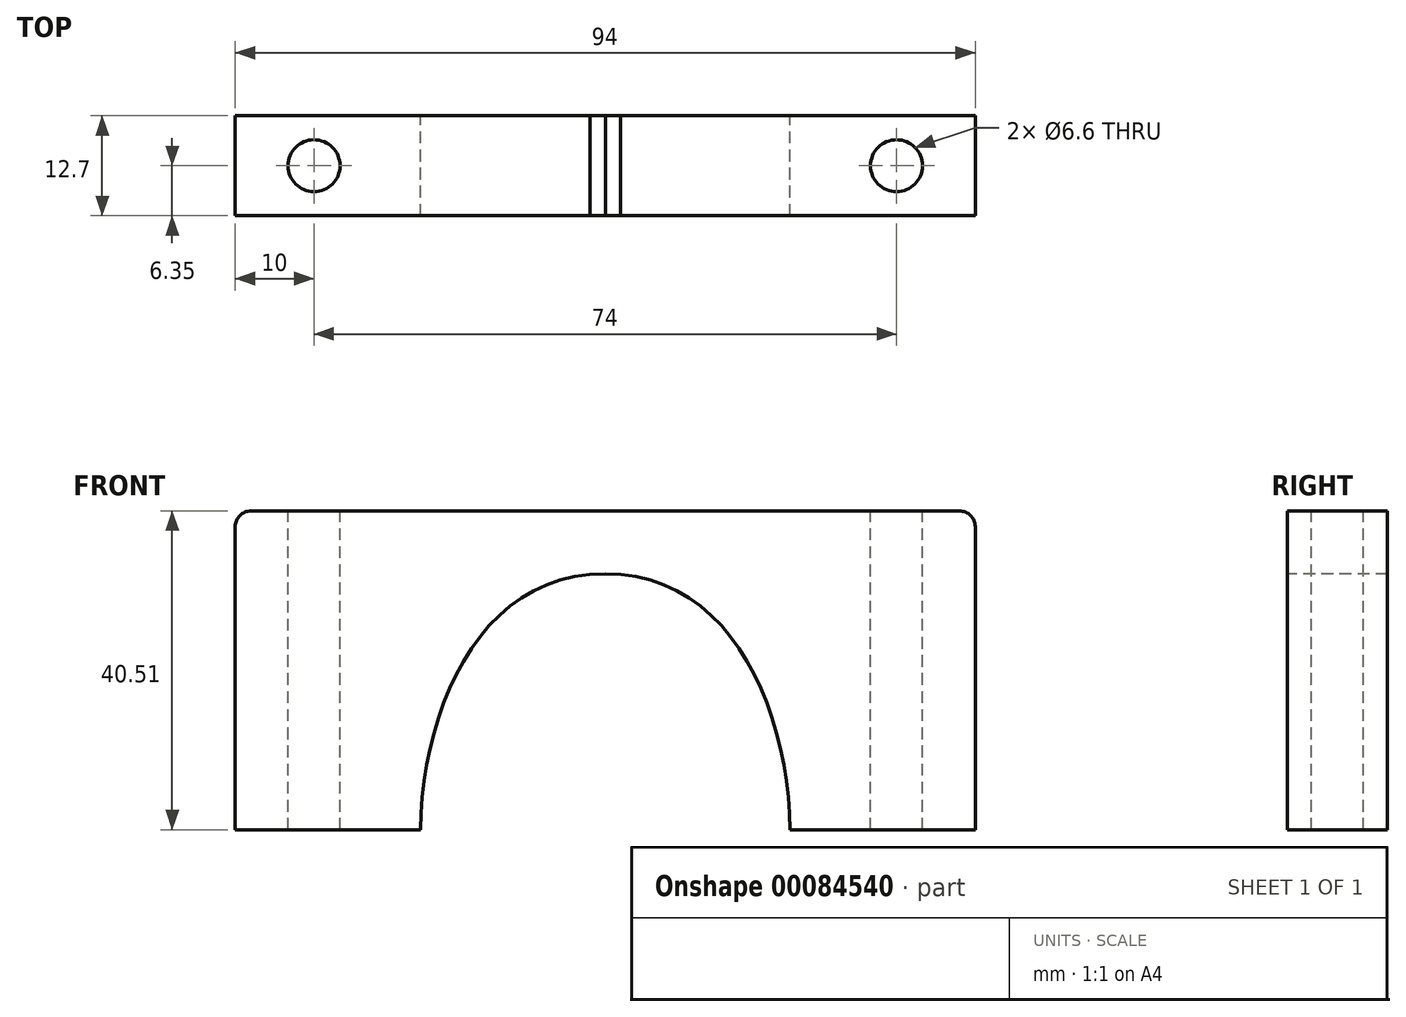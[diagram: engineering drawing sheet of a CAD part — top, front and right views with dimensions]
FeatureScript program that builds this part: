
annotation { "Feature Type Name" : "Feature", "Feature Type Description" : "" }
export const myFeature = defineFeature(function(context is Context, id is Id, definition is map)
    precondition{}
    {
        {
            var Q0;
            Q0=qCreatedBy(makeId("Front.planeOp"),FACE);
            var sketch = newSketch(context, id + "F0", { "sketchPlane" : qUnion([Q0]) });
            skPoint(sketch, "E0", {"position": v(0.8, 9.7) * mm});
            skPoint(sketch, "E1", {"position": v(2.4, 15.7) * mm});
            skPoint(sketch, "E2", {"position": v(6.6, 23.8) * mm});
            skPoint(sketch, "E3", {"position": v(12.9, 30.8) * mm});
            skPoint(sketch, "E4", {"position": v(19, 33.2) * mm});
            skPoint(sketch, "E5", {"position": v(23.5, 33.5) * mm});
            skLineSegment(sketch, "E6", {"start": v(23.5, 33.5) * mm, "end": v(23.5, 0) * mm, "construction": true});
            skPoint(sketch, "E7", {"position": v(3.4, 18.7) * mm});
            skPoint(sketch, "E8", {"position": v(9.6, 28) * mm});
            skFitSpline(sketch, "E9", {"points": [v(0, 0) * mm, v(23.5, 33.5) * mm], "startDerivative": vector(0, 48.1) * mm, "endDerivative": vector(48.2, -0.45) * mm});
            skFitSpline(sketch, "E10.MirrorCS", {"points": [v(47, 0) * mm, v(23.5, 33.5) * mm], "startDerivative": vector(0, 48.1) * mm, "endDerivative": vector(-48.2, -0.45) * mm});
            skFitSpline(sketch, "E11.0", {"points": [v(55, 0) * mm, v(55, 2.31) * mm, v(54.73, 6.98) * mm, v(53.5, 13.94) * mm, v(51.4, 20.7) * mm, v(48.31, 27.06) * mm, v(44.78, 31.86) * mm, v(41.28, 35.2) * mm, v(38.3, 37.4) * mm, v(34.99, 39.2) * mm, v(31.37, 40.54) * mm, v(27.5, 41.35) * mm, v(24.8, 41.51) * mm, v(23.42, 41.5) * mm]});
            skFitSpline(sketch, "E11.1", {"points": [v(-8, 0) * mm, v(-8, 2.31) * mm, v(-7.73, 6.98) * mm, v(-6.5, 13.94) * mm, v(-4.4, 20.7) * mm, v(-1.31, 27.06) * mm, v(2.22, 31.86) * mm, v(5.72, 35.2) * mm, v(8.7, 37.4) * mm, v(12.01, 39.2) * mm, v(15.63, 40.54) * mm, v(19.5, 41.35) * mm, v(22.2, 41.51) * mm, v(23.58, 41.5) * mm]});
            skLineSegment(sketch, "E12", {"start": v(0, 0) * mm, "end": v(-8, 0) * mm});
            skLineSegment(sketch, "E13.MirrorCS", {"start": v(47, 0) * mm, "end": v(55, 0) * mm});
            skLineSegment(sketch, "E14", {"start": v(-7.16, 10) * mm, "end": v(-23.5, 10) * mm});
            skLineSegment(sketch, "E15", {"start": v(-8, 0) * mm, "end": v(-23.5, 0) * mm});
            skLineSegment(sketch, "E16", {"start": v(-23.5, 0) * mm, "end": v(-23.5, 10) * mm});
            skLineSegment(sketch, "E17.MirrorCS", {"start": v(54.16, 10) * mm, "end": v(70.5, 10) * mm});
            skLineSegment(sketch, "E18.MirrorCS", {"start": v(70.5, 0) * mm, "end": v(70.5, 10) * mm});
            skLineSegment(sketch, "E19.MirrorCS", {"start": v(55, 0) * mm, "end": v(70.5, 0) * mm});
            skLineSegment(sketch, "E20", {"start": v(-23.5, 10) * mm, "end": v(-23.5, 41.5) * mm});
            skLineSegment(sketch, "E21", {"start": v(-23.5, 41.5) * mm, "end": v(23.5, 41.5) * mm});
            skLineSegment(sketch, "E22.MirrorCS", {"start": v(70.5, 10) * mm, "end": v(70.5, 41.5) * mm});
            skLineSegment(sketch, "E23.MirrorCS", {"start": v(70.5, 41.5) * mm, "end": v(23.5, 41.5) * mm});
            skSolve(sketch);
        }
        {
            var Q0;
            Q0=qSketchRegion(id+"F0",true);
            extrude(context, id + "F1", {"entities" : qUnion([Q0]), "depth" : 12.7 * mm});
        }
        {
            var Q0;
            Q0=makeQuery(id+"F1.opExtrude","SWEPT_FACE",FACE,{"disambiguationData":[OSD([sQuery(id+"F0.wireOp",EDGE,"E21")])]});
            var sketch = newSketch(context, id + "F2", { "sketchPlane" : qUnion([Q0]) });
            skCircle(sketch, "E24", {"center": v(-13.5, -6.35) * mm, "radius": 3.3 * mm});
            skPoint(sketch, "E24.centerSnap0", {"position": v(-23.5, -6.35) * mm});
            skCircle(sketch, "E25", {"center": v(60.5, -6.35) * mm, "radius": 3.3 * mm});
            skFitSpline(sketch, "E26.0", {"points": [v(23.5, -12.7) * mm, v(23.5, -8.47) * mm, v(23.5, -4.23) * mm, v(23.5, 0) * mm], "construction": true});
            skLineSegment(sketch, "E27.0", {"start": v(-23.5, 0) * mm, "end": v(23.1, 0) * mm});
            skLineSegment(sketch, "E27.1", {"start": v(-23.5, -12.7) * mm, "end": v(-23.5, 0) * mm});
            skLineSegment(sketch, "E27.2", {"start": v(-23.5, -12.7) * mm, "end": v(23.1, -12.7) * mm});
            skLineSegment(sketch, "E28", {"start": v(23.1, 0) * mm, "end": v(23.5, 0) * mm});
            skSolve(sketch);
        }
        {
            var Q0;
            Q0 = qSketchRegion(id + "F2", true);
            var Q1;
            Q1=makeQuery(id+"F1.opExtrude","SWEPT_FACE",FACE,{"disambiguationData":[OSD([sQuery(id+"F0.wireOp",EDGE,"E13.MirrorCS"),sQuery(id+"F0.wireOp",EDGE,"E19.MirrorCS")])]});
            extrude(context, id + "F3", {"entities" : qUnion([Q0]), "operationType" : NewBodyOperationType.REMOVE, "endBound" : BoundingType.UP_TO_SURFACE, "oppositeDirection" : true, "endBoundEntityFace" : qUnion([Q1]), "depth" : 100 * mm});
        }
        {
            var Q0;
            Q0=qCreatedBy(makeId("Front.planeOp"),FACE);
            var sketch = newSketch(context, id + "F4", { "sketchPlane" : qUnion([Q0]) });
            skLineSegment(sketch, "E29.bottom", {"start": v(-28.13, 1) * mm, "end": v(73.94, 1) * mm});
            skLineSegment(sketch, "E29.top", {"start": v(-28.13, -2.48) * mm, "end": v(73.94, -2.48) * mm});
            skLineSegment(sketch, "E29.left", {"start": v(-28.13, 1) * mm, "end": v(-28.13, -2.48) * mm});
            skLineSegment(sketch, "E29.right", {"start": v(73.94, 1) * mm, "end": v(73.94, -2.48) * mm});
            skSolve(sketch);
        }
        {
            var Q0;
            Q0=qSketchRegion(id+"F4",true);
            extrude(context, id + "F5", {"entities" : qUnion([Q0]), "operationType" : NewBodyOperationType.REMOVE, "depth" : 25 * mm});
        }
        {
            var Q0;
            Q0=makeQuery(id+"F1.opExtrude","SWEPT_EDGE",EDGE,{"disambiguationData":[OSD([sQuery(id+"F0.wireOp",EDGE,"E22.MirrorCS"),sQuery(id+"F0.wireOp",EDGE,"E23.MirrorCS")])]});
            var Q1;
            Q1=makeQuery(id+"F1.opExtrude","SWEPT_EDGE",EDGE,{"disambiguationData":[OSD([sQuery(id+"F0.wireOp",EDGE,"E20"),sQuery(id+"F0.wireOp",EDGE,"E21")])]});
            fillet(context, id + "F6", {"entities" : qUnion([Q0, Q1]), "radius" : 2 * mm, "tangentPropagation" : true, "conicFillet" : false});
        }
    });
